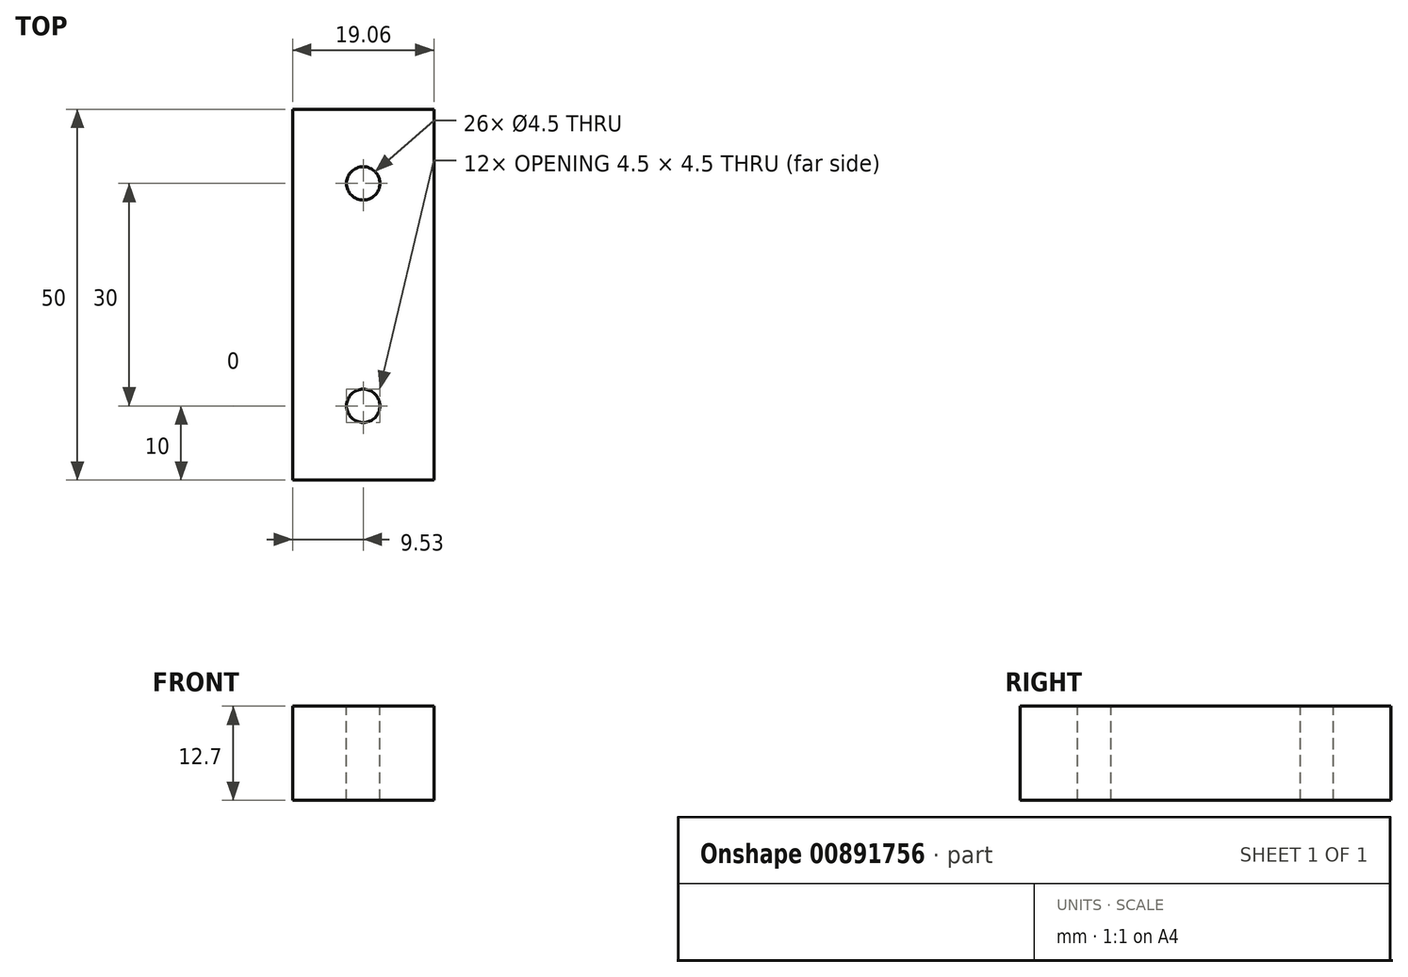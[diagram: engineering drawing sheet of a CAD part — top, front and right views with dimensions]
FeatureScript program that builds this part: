
annotation { "Feature Type Name" : "Feature", "Feature Type Description" : "" }
export const myFeature = defineFeature(function(context is Context, id is Id, definition is map)
    precondition{}
    {
        {
            var Q0;
            Q0=qCreatedBy(makeId("Front.planeOp"),FACE);
            var sketch = newSketch(context, id + "F0", { "sketchPlane" : qUnion([Q0])});
            skLineSegment(sketch, "E0.bottom", {"start": v(9.53, -6.35) * mm, "end": v(-9.52, -6.35) * mm});
            skLineSegment(sketch, "E0.top", {"start": v(9.53, 6.35) * mm, "end": v(-9.53, 6.35) * mm});
            skLineSegment(sketch, "E0.left", {"start": v(9.53, -6.35) * mm, "end": v(9.53, 6.35) * mm});
            skLineSegment(sketch, "E0.right", {"start": v(-9.52, -6.35) * mm, "end": v(-9.53, 6.35) * mm});
            skPoint(sketch, "E0.middle", {"position": v(0, 0) * mm});
            skSolve(sketch);
        }
        {
            var Q0;
            Q0=makeQuery(id+"F0.imprint","IMPRINT",FACE,{"disambiguationData":[TD([[makeQuery(id+"F0.imprint","IMPRINT",EDGE,{"derivedFrom":sQuery(id+"F0.wireOp",EDGE,"E0.bottom")}),-1.0]])]});
            extrude(context, id + "F1", {"entities" : qUnion([Q0]), "endBound" : BoundingType.SYMMETRIC, "depth" : 50 * mm, "offsetDistance" : 25 * mm});
        }
        {
            var Q0;
            Q0=makeQuery(id+"F1.opExtrude","SWEPT_FACE",FACE,{"disambiguationData":[OSD([sQuery(id+"F0.wireOp",EDGE,"E0.top")])]});
            var sketch = newSketch(context, id + "F2", { "sketchPlane" : qUnion([Q0])});
            skPoint(sketch, "E1", {"position": v(0, 15) * mm});
            skPoint(sketch, "E2.MirrorP", {"position": v(0, -15) * mm});
            skSolve(sketch);
        }
        {
            var Q0;
            Q0=sQuery(id+"F2.wireOp",VERTEX,"E1");
            var Q1;
            Q1=sQuery(id+"F2.wireOp",VERTEX,"E2.MirrorP");
            var Q2;
            Q2=makeQuery(id+"F1.opExtrude","SWEPT_BODY",BODY,{"disambiguationData":[OSD([sQuery(id+"F0.wireOp",EDGE,"E0.bottom"),sQuery(id+"F0.wireOp",EDGE,"E0.top"),sQuery(id+"F0.wireOp",EDGE,"E0.left"),sQuery(id+"F0.wireOp",EDGE,"E0.right")])]});
            hole(context, id + "F3", {"style" : HoleStyle.SIMPLE, "endStyle" : HoleEndStyle.THROUGH, "standardTappedOrClearance" : lookupTablePath({ "standard" : "ISO", "engagement" : "50%", "pitch" : "0.8 mm", "size" : "M5", "type" : "Tapped" }), "standardBlindInLast" : lookupTablePath({ "standard" : "ISO", "engagement" : "50%", "pitch" : "0.8 mm", "size" : "M5", "type" : "Tapped" }), "holeDiameter" : 4.5 * mm, "majorDiameter" : 5 * mm, "showTappedDepth" : true, "isTappedThrough" : true, "tappedDepth" : 7.9 * mm, "tapClearance" : 3, "startFromSketch" : true, "locations" : qUnion([Q0, Q1]), "scope" : qUnion([Q2])});
        }
    });
